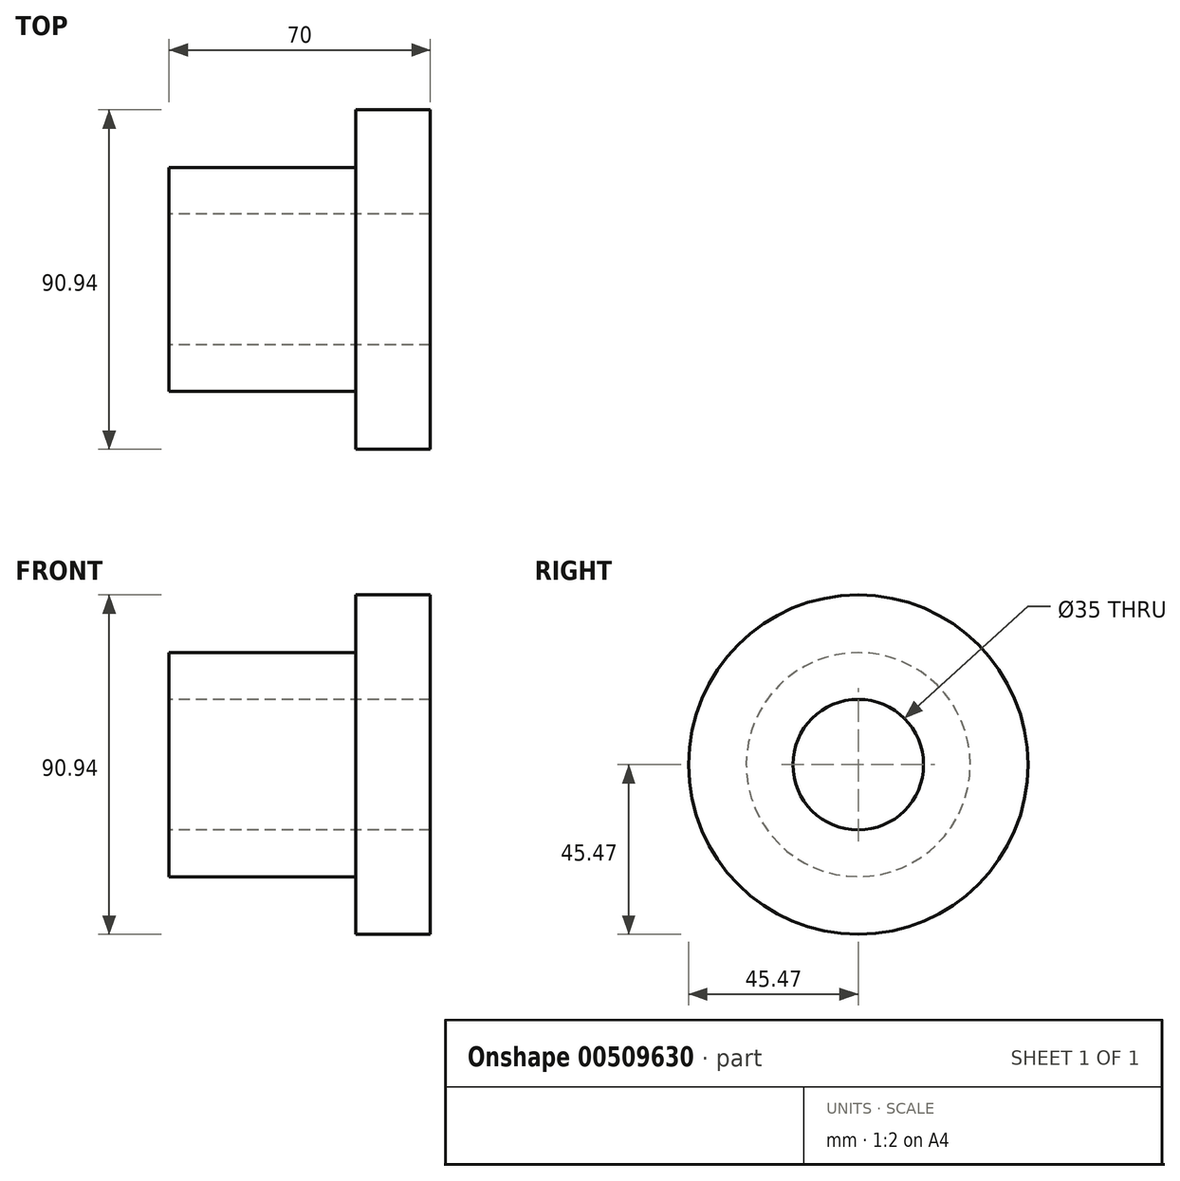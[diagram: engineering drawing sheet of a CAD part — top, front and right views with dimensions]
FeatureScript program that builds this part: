
annotation { "Feature Type Name" : "Feature", "Feature Type Description" : "" }
export const myFeature = defineFeature(function(context is Context, id is Id, definition is map)
    precondition{}
    {
        {
            var Q0;
            Q0=qCreatedBy(makeId("Front.planeOp"),FACE);
            var sketch = newSketch(context, id + "F0", { "sketchPlane" : qUnion([Q0])});
            skLineSegment(sketch, "E0", {"start": v(-44.97, 0) * mm, "end": v(25.03, 0) * mm, "construction": true});
            skLineSegment(sketch, "E1", {"start": v(-44.97, 17.5) * mm, "end": v(25.03, 17.5) * mm});
            skLineSegment(sketch, "E2", {"start": v(25.03, 17.5) * mm, "end": v(25.03, 45.47) * mm});
            skLineSegment(sketch, "E3", {"start": v(25.03, 45.47) * mm, "end": v(5.03, 45.47) * mm});
            skLineSegment(sketch, "E4", {"start": v(5.03, 45.47) * mm, "end": v(5.03, 30) * mm});
            skLineSegment(sketch, "E5", {"start": v(5.03, 30) * mm, "end": v(-44.97, 30) * mm});
            skLineSegment(sketch, "E6", {"start": v(-44.97, 30) * mm, "end": v(-44.97, 17.5) * mm});
            skSolve(sketch);
        }
        {
            var Q0;
            Q0=makeQuery(id+"F0.imprint","IMPRINT",FACE,{"disambiguationData":[TD([[makeQuery(id+"F0.imprint","IMPRINT",EDGE,{"derivedFrom":sQuery(id+"F0.wireOp",EDGE,"E1")}),1.0]])]});
            var Q1;
            Q1=sQuery(id+"F0.wireOp",EDGE,"E0");
            revolve(context, id + "F1", {"entities" : qUnion([Q0]), "axis" : qUnion([Q1]), "revolveType" : RevolveType.FULL});
        }
    });
